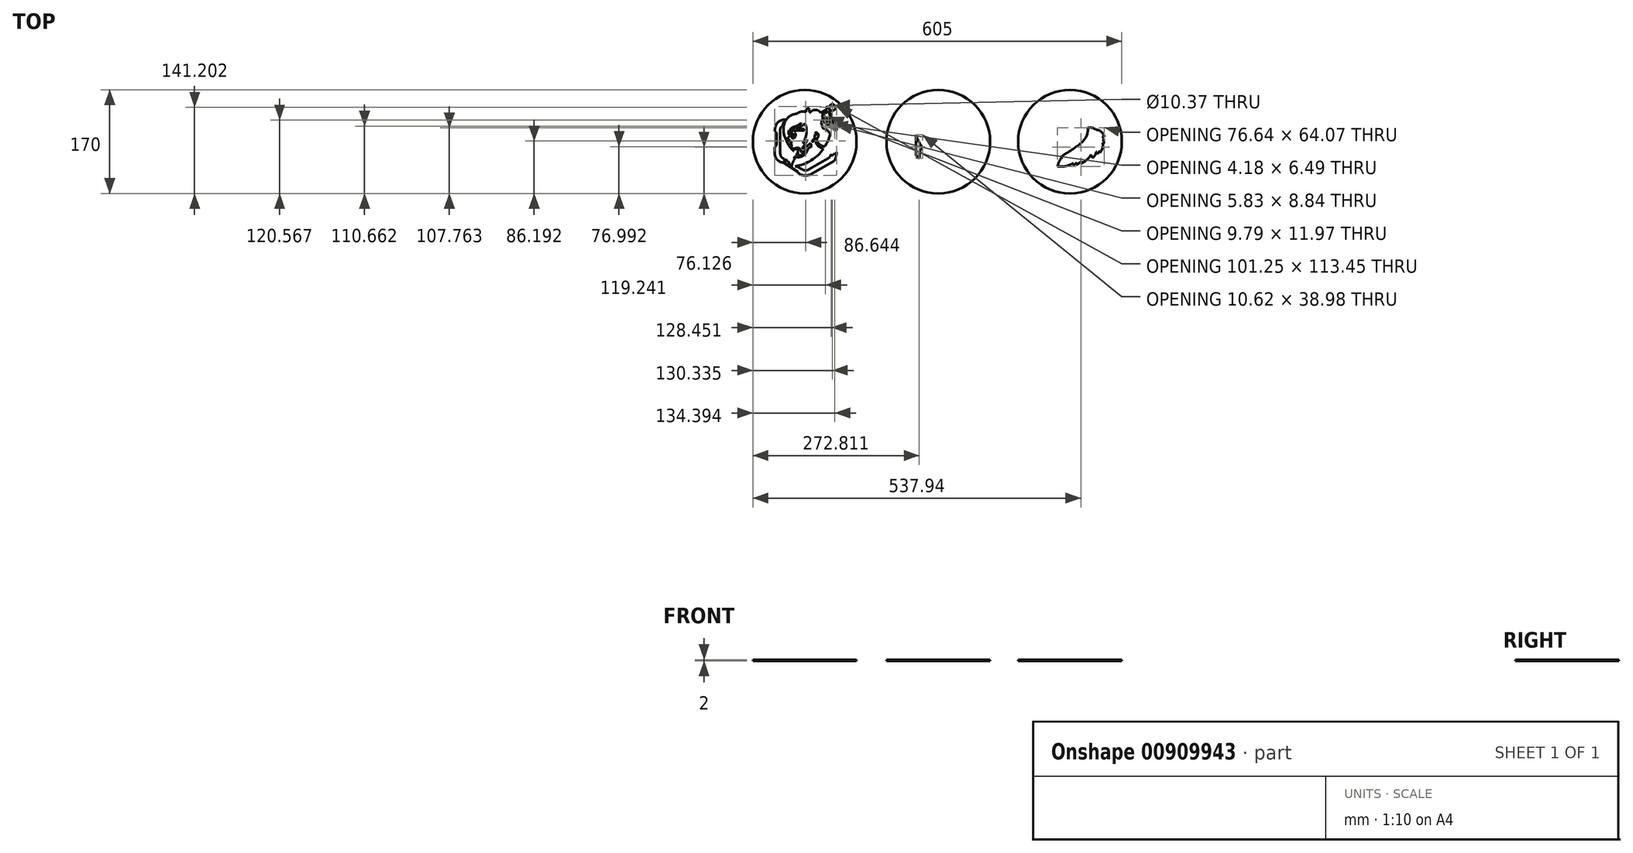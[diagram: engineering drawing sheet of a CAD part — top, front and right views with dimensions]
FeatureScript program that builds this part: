
annotation { "Feature Type Name" : "Feature", "Feature Type Description" : "" }
export const myFeature = defineFeature(function(context is Context, id is Id, definition is map)
    precondition{}
    {
        {
            var Q0;
            Q0=qCreatedBy(makeId("Top.planeOp"),FACE);
            var sketch = newSketch(context, id + "F0", { "sketchPlane" : qUnion([Q0])});
            skArc(sketch, "E0", {"start": v(2.98, 20.38) * mm, "mid": v(2.27, 25.4) * mm, "end": v(0, 29.95) * mm});
            skLineSegment(sketch, "E1", {"start": v(-0.76, 20.69) * mm, "end": v(-13.48, 21.74) * mm});
            skLineSegment(sketch, "E2", {"start": v(-13.48, 21.74) * mm, "end": v(-13.48, 22.74) * mm});
            skLineSegment(sketch, "E3", {"start": v(-13.48, 22.74) * mm, "end": v(-19.26, 22.4) * mm});
            skArc(sketch, "E4", {"start": v(-19.26, 22.4) * mm, "mid": v(-20.2, 21.9) * mm, "end": v(-20.45, 20.84) * mm});
            skArc(sketch, "E5", {"start": v(-20.45, 20.84) * mm, "mid": v(-21.5, 20.38) * mm, "end": v(-22.23, 19.5) * mm});
            skArc(sketch, "E6", {"start": v(-22.91, 18.23) * mm, "mid": v(-22.3, 18.72) * mm, "end": v(-22.23, 19.5) * mm});
            skArc(sketch, "E7", {"start": v(-23.6, 19.5) * mm, "mid": v(-23.46, 18.75) * mm, "end": v(-22.91, 18.23) * mm});
            skArc(sketch, "E8", {"start": v(-24.08, 19.84) * mm, "mid": v(-23.94, 19.54) * mm, "end": v(-23.6, 19.5) * mm});
            skArc(sketch, "E9", {"start": v(-16.32, 24.77) * mm, "mid": v(-20.62, 22.98) * mm, "end": v(-24.08, 19.84) * mm});
            skArc(sketch, "E10", {"start": v(-16.32, 24.77) * mm, "mid": v(-10.63, 27.32) * mm, "end": v(-5.77, 31.23) * mm});
            skArc(sketch, "E11", {"start": v(-12.06, 23.5) * mm, "mid": v(-8.03, 26.64) * mm, "end": v(-5.77, 31.23) * mm});
            skArc(sketch, "E12", {"start": v(-12.06, 23.5) * mm, "mid": v(-5.35, 25.44) * mm, "end": v(0, 29.95) * mm});
            skArc(sketch, "E13", {"start": v(-3.23, -2.27) * mm, "mid": v(1.52, 6.95) * mm, "end": v(3.03, 17.2) * mm});
            skArc(sketch, "E14", {"start": v(-3.23, -2.27) * mm, "mid": v(1.12, -0.57) * mm, "end": v(4.2, 2.96) * mm});
            skArc(sketch, "E15", {"start": v(-4.8, -11.32) * mm, "mid": v(0.43, -4.63) * mm, "end": v(4.2, 2.96) * mm});
            skArc(sketch, "E16", {"start": v(-4.8, -11.32) * mm, "mid": v(3.01, -7.8) * mm, "end": v(9.56, -2.27) * mm});
            skArc(sketch, "E17", {"start": v(9.56, -2.27) * mm, "mid": v(9.67, -2.93) * mm, "end": v(9.82, -3.57) * mm});
            skArc(sketch, "E18", {"start": v(29.41, 22.54) * mm, "mid": v(28.46, 27.03) * mm, "end": v(26.58, 31.23) * mm});
            skArc(sketch, "E19", {"start": v(26.58, 31.23) * mm, "mid": v(29.35, 37.4) * mm, "end": v(28.2, 44.07) * mm});
            skLineSegment(sketch, "E20", {"start": v(28.2, 44.07) * mm, "end": v(38.69, 50.4) * mm});
            skLineSegment(sketch, "E21", {"start": v(38.69, 50.4) * mm, "end": v(40.82, 46.88) * mm});
            skLineSegment(sketch, "E22", {"start": v(40.82, 46.88) * mm, "end": v(42.94, 48.16) * mm});
            skLineSegment(sketch, "E23", {"start": v(42.94, 48.16) * mm, "end": v(38.69, 57.92) * mm});
            skLineSegment(sketch, "E24", {"start": v(38.69, 57.92) * mm, "end": v(35.35, 56.46) * mm});
            skArc(sketch, "E25", {"start": v(35.35, 56.46) * mm, "mid": v(35.57, 55.64) * mm, "end": v(36.4, 55.44) * mm});
            skArc(sketch, "E26", {"start": v(36.4, 53.18) * mm, "mid": v(36.82, 54.31) * mm, "end": v(36.4, 55.44) * mm});
            skLineSegment(sketch, "E27", {"start": v(36.4, 53.18) * mm, "end": v(26.24, 47.39) * mm});
            skArc(sketch, "E28", {"start": v(26.24, 47.39) * mm, "mid": v(17.58, 52.34) * mm, "end": v(8.92, 47.39) * mm});
            skArc(sketch, "E29", {"start": v(7.13, 54.78) * mm, "mid": v(7.26, 50.9) * mm, "end": v(8.92, 47.39) * mm});
            skArc(sketch, "E30", {"start": v(7.13, 54.78) * mm, "mid": v(2.96, 53.06) * mm, "end": v(2.42, 48.6) * mm});
            skArc(sketch, "E31", {"start": v(2.42, 48.6) * mm, "mid": v(-5.84, 49.25) * mm, "end": v(-13.28, 45.63) * mm});
            skArc(sketch, "E32", {"start": v(-13.28, 45.63) * mm, "mid": v(-25.51, 41.11) * mm, "end": v(-33.09, 30.5) * mm});
            skArc(sketch, "E33", {"start": v(-33.09, 30.5) * mm, "mid": v(-34.85, 17.73) * mm, "end": v(-31.54, 5.27) * mm});
            skArc(sketch, "E34", {"start": v(-31.54, 5.27) * mm, "mid": v(-26.16, -5.74) * mm, "end": v(-18.36, -15.2) * mm});
            skArc(sketch, "E35", {"start": v(-18.36, -12.38) * mm, "mid": v(-18.83, -13.79) * mm, "end": v(-18.36, -15.2) * mm});
            skArc(sketch, "E36", {"start": v(-9.8, -12.01) * mm, "mid": v(-14.1, -11.83) * mm, "end": v(-18.36, -12.38) * mm});
            skArc(sketch, "E37", {"start": v(-9.8, -12.01) * mm, "mid": v(-11.09, -16.15) * mm, "end": v(-11.15, -20.49) * mm});
            skArc(sketch, "E38", {"start": v(-12.15, -19.1) * mm, "mid": v(-11.73, -19.85) * mm, "end": v(-11.15, -20.49) * mm});
            skArc(sketch, "E39", {"start": v(-12.15, -19.1) * mm, "mid": v(-12.83, -19.17) * mm, "end": v(-12.84, -19.85) * mm});
            skPoint(sketch, "E39.endSnap0", {"position": v(-11.73, -19.85) * mm});
            skArc(sketch, "E40", {"start": v(-12.45, -21.26) * mm, "mid": v(-12.17, -20.42) * mm, "end": v(-12.84, -19.85) * mm});
            skArc(sketch, "E41", {"start": v(-12.45, -21.26) * mm, "mid": v(-13.16, -21.69) * mm, "end": v(-13.85, -22.17) * mm});
            skLineSegment(sketch, "E42", {"start": v(-17.55, -26.74) * mm, "end": v(-16.32, -26.74) * mm});
            skArc(sketch, "E43", {"start": v(-15.64, -27.26) * mm, "mid": v(-15.9, -26.89) * mm, "end": v(-16.32, -26.74) * mm});
            skArc(sketch, "E44", {"start": v(-15.64, -27.26) * mm, "mid": v(-19.4, -33.43) * mm, "end": v(-21.53, -40.35) * mm});
            skArc(sketch, "E45", {"start": v(-21.53, -40.35) * mm, "mid": v(-22.46, -40.14) * mm, "end": v(-23.4, -40.35) * mm});
            skArc(sketch, "E46", {"start": v(-26.13, -32.33) * mm, "mid": v(-25.18, -36.48) * mm, "end": v(-23.4, -40.35) * mm});
            skArc(sketch, "E47", {"start": v(-15.43, -40.35) * mm, "mid": v(10.63, -30.47) * mm, "end": v(30.92, -11.35) * mm});
            skPoint(sketch, "E47.startSnap0", {"position": v(-15.43, -23.6) * mm});
            skArc(sketch, "E48", {"start": v(41.98, 12.7) * mm, "mid": v(36.6, 18.76) * mm, "end": v(29.41, 22.54) * mm});
            skArc(sketch, "E49", {"start": v(-5.53, -17.95) * mm, "mid": v(-1.98, -15.79) * mm, "end": v(1.56, -13.61) * mm});
            skArc(sketch, "E50", {"start": v(-5.53, -17.95) * mm, "mid": v(-6.68, -13.86) * mm, "end": v(-9.17, -10.41) * mm});
            skArc(sketch, "E51", {"start": v(-9.17, -10.41) * mm, "mid": v(-13.14, -10.14) * mm, "end": v(-16.96, -11.28) * mm});
            skArc(sketch, "E52", {"start": v(-21.82, -7.68) * mm, "mid": v(-20.34, -10.76) * mm, "end": v(-16.96, -11.28) * mm});
            skArc(sketch, "E53", {"start": v(-21.82, -7.68) * mm, "mid": v(-21.6, -5.4) * mm, "end": v(-23.38, -3.97) * mm});
            skArc(sketch, "E54", {"start": v(-20.88, -1.47) * mm, "mid": v(-22.32, -2.53) * mm, "end": v(-23.38, -3.97) * mm});
            skArc(sketch, "E55", {"start": v(-24.72, 0) * mm, "mid": v(-22.93, -1.07) * mm, "end": v(-20.88, -1.47) * mm});
            skArc(sketch, "E56", {"start": v(-24.72, 1.38) * mm, "mid": v(-24.9, 0.69) * mm, "end": v(-24.72, 0) * mm});
            skArc(sketch, "E57", {"start": v(-24.72, 1.38) * mm, "mid": v(-24.75, 2.75) * mm, "end": v(-26, 3.32) * mm});
            skArc(sketch, "E58", {"start": v(-27.8, 5.27) * mm, "mid": v(-27.2, 4.02) * mm, "end": v(-26, 3.32) * mm});
            skArc(sketch, "E59", {"start": v(-27.02, 7) * mm, "mid": v(-27.66, 6.25) * mm, "end": v(-27.8, 5.27) * mm});
            skArc(sketch, "E60", {"start": v(-27.02, 7) * mm, "mid": v(-24.92, 8.65) * mm, "end": v(-23.38, 10.84) * mm});
            skArc(sketch, "E61", {"start": v(-23.38, 10.84) * mm, "mid": v(-23.26, 11.1) * mm, "end": v(-23.16, 11.35) * mm});
            skArc(sketch, "E62", {"start": v(-21.62, 14.34) * mm, "mid": v(-22.16, 14.77) * mm, "end": v(-22.7, 14.34) * mm});
            skArc(sketch, "E63", {"start": v(-20.89, 6.61) * mm, "mid": v(-19.1, 5.43) * mm, "end": v(-17.06, 6.08) * mm});
            skArc(sketch, "E64", {"start": v(-21.62, 14.34) * mm, "mid": v(-21.93, 10.41) * mm, "end": v(-20.89, 6.61) * mm});
            skArc(sketch, "E65", {"start": v(-17.06, 6.08) * mm, "mid": v(-15.29, 9.27) * mm, "end": v(-15.17, 12.93) * mm});
            skArc(sketch, "E66", {"start": v(-14.67, 17.82) * mm, "mid": v(-14.93, 17.28) * mm, "end": v(-15.14, 16.7) * mm});
            skArc(sketch, "E67", {"start": v(-12.8, 18.66) * mm, "mid": v(-13.88, 18.56) * mm, "end": v(-14.67, 17.82) * mm});
            skArc(sketch, "E68", {"start": v(-23.8, 17.14) * mm, "mid": v(-24.94, 18.36) * mm, "end": v(-26.16, 17.22) * mm});
            skArc(sketch, "E69", {"start": v(-26.1, 12.66) * mm, "mid": v(-26.07, 12.44) * mm, "end": v(-26, 12.23) * mm});
            skArc(sketch, "E70", {"start": v(-26.16, 17.22) * mm, "mid": v(-26.23, 14.94) * mm, "end": v(-26.1, 12.66) * mm});
            skArc(sketch, "E71", {"start": v(-26, 12.23) * mm, "mid": v(-25.21, 11.3) * mm, "end": v(-24.08, 11.73) * mm});
            skPoint(sketch, "E72.orphan", {"position": v(-26.1, 12.95) * mm});
            skPoint(sketch, "E73.trimOffspring.end.orphan", {"position": v(-26.16, 16.74) * mm});
            skLineSegment(sketch, "E74", {"start": v(-20.98, 18.42) * mm, "end": v(-17.32, 19.65) * mm});
            skArc(sketch, "E75", {"start": v(-16.9, 9.64) * mm, "mid": v(-16.69, 11.85) * mm, "end": v(-16.64, 14.07) * mm});
            skArc(sketch, "E76", {"start": v(-20.98, 18.42) * mm, "mid": v(-21.19, 16.1) * mm, "end": v(-21.11, 13.77) * mm});
            skArc(sketch, "E77", {"start": v(-20.43, 9.46) * mm, "mid": v(-19.92, 8.27) * mm, "end": v(-19.04, 7.32) * mm});
            skArc(sketch, "E78", {"start": v(-21.11, 13.77) * mm, "mid": v(-20.93, 11.59) * mm, "end": v(-20.43, 9.46) * mm});
            skArc(sketch, "E79.trimOffspring", {"start": v(-19.04, 7.32) * mm, "mid": v(-18.14, 7.44) * mm, "end": v(-17.52, 8.1) * mm});
            skArc(sketch, "E80", {"start": v(-17.52, 8.1) * mm, "mid": v(-17.13, 8.83) * mm, "end": v(-16.9, 9.64) * mm});
            skPoint(sketch, "E81.orphan", {"position": v(-18.02, 7.5) * mm});
            skArc(sketch, "E82", {"start": v(20.04, 10.77) * mm, "mid": v(18.73, 11.71) * mm, "end": v(17.12, 11.89) * mm});
            skArc(sketch, "E83", {"start": v(20.04, 10.77) * mm, "mid": v(19.47, 12.9) * mm, "end": v(17.45, 13.8) * mm});
            skArc(sketch, "E84", {"start": v(14.22, 4.55) * mm, "mid": v(15.76, 4.6) * mm, "end": v(16.7, 5.83) * mm});
            skArc(sketch, "E85", {"start": v(17.15, 4.86) * mm, "mid": v(17.04, 5.4) * mm, "end": v(16.7, 5.83) * mm});
            skArc(sketch, "E86", {"start": v(17.15, 4.86) * mm, "mid": v(17.22, 6.61) * mm, "end": v(15.97, 7.85) * mm});
            skArc(sketch, "E87", {"start": v(15.97, 7.85) * mm, "mid": v(16.75, 9.8) * mm, "end": v(17.12, 11.89) * mm});
            skArc(sketch, "E88", {"start": v(12.05, 0.73) * mm, "mid": v(13.2, 2.6) * mm, "end": v(14.22, 4.55) * mm});
            skArc(sketch, "E89", {"start": v(12.05, 0.73) * mm, "mid": v(12.93, 0.14) * mm, "end": v(13.8, 0.73) * mm});
            skArc(sketch, "E90", {"start": v(13.8, 0.73) * mm, "mid": v(14.42, 0.93) * mm, "end": v(15.02, 1.15) * mm});
            skArc(sketch, "E91", {"start": v(20.83, 5.54) * mm, "mid": v(22.22, 8.7) * mm, "end": v(22.26, 12.17) * mm});
            skArc(sketch, "E92", {"start": v(22.26, 12.17) * mm, "mid": v(20.38, 14.41) * mm, "end": v(17.6, 15.3) * mm});
            skArc(sketch, "E93", {"start": v(17.6, 15.3) * mm, "mid": v(17.4, 14.56) * mm, "end": v(17.45, 13.8) * mm});
            skLineSegment(sketch, "E94", {"start": v(-15.43, -40.35) * mm, "end": v(-11.75, -41.2) * mm});
            skLineSegment(sketch, "E95", {"start": v(-11.75, -41.2) * mm, "end": v(-3.7, -45.74) * mm});
            skLineSegment(sketch, "E96", {"start": v(7.07, -45.34) * mm, "end": v(38.43, -27.31) * mm});
            skArc(sketch, "E97", {"start": v(-3.7, -45.74) * mm, "mid": v(1.74, -47.07) * mm, "end": v(7.07, -45.34) * mm});
            skArc(sketch, "E98", {"start": v(38.43, -27.31) * mm, "mid": v(41.3, -24.72) * mm, "end": v(42.86, -21.17) * mm});
            skArc(sketch, "E99", {"start": v(42.86, -21.17) * mm, "mid": v(44.47, -22.27) * mm, "end": v(46.43, -22.16) * mm});
            skArc(sketch, "E100", {"start": v(48.13, -20) * mm, "mid": v(46.96, -20.83) * mm, "end": v(46.43, -22.16) * mm});
            skArc(sketch, "E101", {"start": v(48.13, -20) * mm, "mid": v(50.42, -20.15) * mm, "end": v(51.7, -18.24) * mm});
            skArc(sketch, "E102", {"start": v(52.27, -17.15) * mm, "mid": v(51.92, -17.66) * mm, "end": v(51.7, -18.24) * mm});
            skArc(sketch, "E103", {"start": v(49.39, -30.3) * mm, "mid": v(51.58, -23.9) * mm, "end": v(52.27, -17.15) * mm});
            skArc(sketch, "E104", {"start": v(47.66, -31.65) * mm, "mid": v(48.54, -31) * mm, "end": v(49.39, -30.3) * mm});
            skLineSegment(sketch, "E105", {"start": v(47.66, -31.65) * mm, "end": v(13.51, -51.26) * mm});
            skLineSegment(sketch, "E106", {"start": v(-10.87, -51.18) * mm, "end": v(-10.87, -49.26) * mm});
            skLineSegment(sketch, "E107", {"start": v(-10.87, -49.26) * mm, "end": v(-34.95, -34.47) * mm});
            skArc(sketch, "E108", {"start": v(-10.87, -51.18) * mm, "mid": v(1.3, -55.53) * mm, "end": v(13.51, -51.26) * mm});
            skArc(sketch, "E109", {"start": v(-28.4, -31.22) * mm, "mid": v(-27.79, -32.85) * mm, "end": v(-26.13, -32.33) * mm});
            skLineSegment(sketch, "E110", {"start": v(-28.4, -31.22) * mm, "end": v(-32.07, -28.94) * mm});
            skArc(sketch, "E111", {"start": v(-32.07, -33.34) * mm, "mid": v(-31.9, -31.14) * mm, "end": v(-32.07, -28.94) * mm});
            skArc(sketch, "E112", {"start": v(-33.86, -32.4) * mm, "mid": v(-33.43, -33.75) * mm, "end": v(-32.07, -33.34) * mm});
            skArc(sketch, "E113", {"start": v(-33.86, -32.4) * mm, "mid": v(-33.53, -30.33) * mm, "end": v(-33.53, -28.24) * mm});
            skArc(sketch, "E114", {"start": v(-40.08, -19.22) * mm, "mid": v(-38.34, -24.84) * mm, "end": v(-33.53, -28.24) * mm});
            skLineSegment(sketch, "E115", {"start": v(-40.08, -19.22) * mm, "end": v(-40.08, 20.21) * mm});
            skArc(sketch, "E116", {"start": v(-35.96, 26.09) * mm, "mid": v(-38.95, 23.8) * mm, "end": v(-40.08, 20.21) * mm});
            skArc(sketch, "E117", {"start": v(-31.67, 36) * mm, "mid": v(-34.72, 31.43) * mm, "end": v(-35.96, 26.09) * mm});
            skArc(sketch, "E118", {"start": v(-31.67, 36) * mm, "mid": v(-42.48, 33.1) * mm, "end": v(-48.25, 23.52) * mm});
            skArc(sketch, "E119", {"start": v(-48.25, 23.52) * mm, "mid": v(-48.78, 21) * mm, "end": v(-48.98, 18.44) * mm});
            skLineSegment(sketch, "E120", {"start": v(-48.98, 18.44) * mm, "end": v(-47.03, 15.8) * mm});
            skLineSegment(sketch, "E121", {"start": v(-46.25, 13.42) * mm, "end": v(-46.25, -4.36) * mm});
            skLineSegment(sketch, "E122", {"start": v(-47.3, -7.06) * mm, "end": v(-48.98, -8.9) * mm});
            skLineSegment(sketch, "E123", {"start": v(-48.98, -8.9) * mm, "end": v(-48.98, -19.22) * mm});
            skArc(sketch, "E124", {"start": v(-48.98, -19.22) * mm, "mid": v(-44.94, -29.58) * mm, "end": v(-34.95, -34.47) * mm});
            skPoint(sketch, "E125.visualSharp", {"position": v(-46.25, -5.91) * mm});
            skArc(sketch, "E125.filletArc", {"start": v(-47.3, -7.06) * mm, "mid": v(-46.52, -5.8) * mm, "end": v(-46.25, -4.36) * mm});
            skPoint(sketch, "E126.visualSharp", {"position": v(-46.25, 14.74) * mm});
            skArc(sketch, "E126.filletArc", {"start": v(-46.25, 13.42) * mm, "mid": v(-46.45, 14.67) * mm, "end": v(-47.03, 15.8) * mm});
            skCircle(sketch, "E127", {"center": v(45.33, 56.2) * mm, "radius": 5.19 * mm});
            skCircle(sketch, "E128", {"center": v(41.71, 45.04) * mm, "radius": 1.43 * mm});
            skCircle(sketch, "E129", {"center": v(42.55, 40.8) * mm, "radius": 1.63 * mm});
            skCircle(sketch, "E130", {"center": v(42.73, 30.59) * mm, "radius": 1.36 * mm});
            skArc(sketch, "E131", {"start": v(39.12, 32.51) * mm, "mid": v(37.28, 30.85) * mm, "end": v(35.75, 28.9) * mm});
            skArc(sketch, "E132", {"start": v(40.66, 31.51) * mm, "mid": v(39.97, 32.14) * mm, "end": v(39.12, 32.51) * mm});
            skArc(sketch, "E133", {"start": v(40.66, 31.51) * mm, "mid": v(40.66, 30.6) * mm, "end": v(41.1, 29.8) * mm});
            skArc(sketch, "E134", {"start": v(41.1, 29.8) * mm, "mid": v(39.97, 28.87) * mm, "end": v(39.12, 27.69) * mm});
            skArc(sketch, "E135", {"start": v(35.75, 28.9) * mm, "mid": v(37.4, 28.17) * mm, "end": v(39.12, 27.69) * mm});
            skArc(sketch, "E136", {"start": v(42.1, 28.17) * mm, "mid": v(41.71, 26.84) * mm, "end": v(41.36, 25.5) * mm});
            skPoint(sketch, "E136.startSnap0", {"position": v(37.4, 28.17) * mm});
            skArc(sketch, "E137", {"start": v(41.36, 25.5) * mm, "mid": v(42.57, 23.76) * mm, "end": v(44.21, 22.42) * mm});
            skArc(sketch, "E138", {"start": v(44.21, 22.42) * mm, "mid": v(45.09, 24.22) * mm, "end": v(45.54, 26.17) * mm});
            skArc(sketch, "E139", {"start": v(44.21, 28.9) * mm, "mid": v(44.77, 27.48) * mm, "end": v(45.54, 26.17) * mm});
            skArc(sketch, "E140", {"start": v(42.1, 28.17) * mm, "mid": v(43.26, 28.25) * mm, "end": v(44.21, 28.9) * mm});
            skArc(sketch, "E141", {"start": v(45.07, 30.19) * mm, "mid": v(46.37, 29.49) * mm, "end": v(47.73, 28.9) * mm});
            skArc(sketch, "E142", {"start": v(47.73, 28.9) * mm, "mid": v(49.73, 30.45) * mm, "end": v(51.2, 32.51) * mm});
            skArc(sketch, "E143", {"start": v(51.2, 32.51) * mm, "mid": v(49.53, 33.36) * mm, "end": v(47.73, 33.85) * mm});
            skArc(sketch, "E144", {"start": v(47.73, 33.85) * mm, "mid": v(46.31, 33.03) * mm, "end": v(45, 32.06) * mm});
            skArc(sketch, "E145", {"start": v(45.07, 30.19) * mm, "mid": v(45.1, 31.12) * mm, "end": v(45, 32.06) * mm});
            skArc(sketch, "E146", {"start": v(43.31, 33.2) * mm, "mid": v(42.7, 33.42) * mm, "end": v(42.1, 33.15) * mm});
            skArc(sketch, "E147", {"start": v(43.31, 33.2) * mm, "mid": v(43.94, 34.66) * mm, "end": v(44.21, 36.23) * mm});
            skArc(sketch, "E148", {"start": v(42.96, 38.5) * mm, "mid": v(43.41, 37.27) * mm, "end": v(44.21, 36.23) * mm});
            skArc(sketch, "E149", {"start": v(42.96, 38.5) * mm, "mid": v(41.83, 37.21) * mm, "end": v(41.36, 35.57) * mm});
            skArc(sketch, "E150", {"start": v(41.36, 35.57) * mm, "mid": v(41.73, 34.36) * mm, "end": v(42.1, 33.15) * mm});
            skLineSegment(sketch, "E151", {"start": v(41.52, 29.05) * mm, "end": v(39.41, 27.26) * mm});
            skLineSegment(sketch, "E152", {"start": v(39.41, 27.26) * mm, "end": v(39.41, 25.7) * mm});
            skLineSegment(sketch, "E153", {"start": v(39.41, 25.7) * mm, "end": v(40.74, 25.7) * mm});
            skArc(sketch, "E154", {"start": v(41.52, 29.05) * mm, "mid": v(41.1, 27.38) * mm, "end": v(40.74, 25.7) * mm});
            skLineSegment(sketch, "E155", {"start": v(38.98, 33.46) * mm, "end": v(41.36, 32.14) * mm});
            skPoint(sketch, "E155.endSnap0", {"position": v(39.97, 32.14) * mm});
            skLineSegment(sketch, "E156", {"start": v(41.36, 32.14) * mm, "end": v(40.66, 35.06) * mm});
            skLineSegment(sketch, "E157", {"start": v(40.66, 35.06) * mm, "end": v(39.1, 35.18) * mm});
            skLineSegment(sketch, "E158", {"start": v(39.1, 35.18) * mm, "end": v(38.98, 33.46) * mm});
            skLineSegment(sketch, "E159", {"start": v(43.94, 32.53) * mm, "end": v(44.64, 36) * mm});
            skLineSegment(sketch, "E160", {"start": v(44.64, 36) * mm, "end": v(47.12, 37.22) * mm});
            skLineSegment(sketch, "E161", {"start": v(47.12, 37.22) * mm, "end": v(47.06, 34.87) * mm});
            skLineSegment(sketch, "E162", {"start": v(47.06, 34.87) * mm, "end": v(43.94, 32.53) * mm});
            skLineSegment(sketch, "E163", {"start": v(44.71, 29.28) * mm, "end": v(47.75, 28.1) * mm});
            skLineSegment(sketch, "E164", {"start": v(47.75, 28.1) * mm, "end": v(48.1, 26.46) * mm});
            skLineSegment(sketch, "E165", {"start": v(48.1, 26.46) * mm, "end": v(46.18, 26.41) * mm});
            skLineSegment(sketch, "E166", {"start": v(46.18, 26.41) * mm, "end": v(44.71, 29.28) * mm});
            skArc(sketch, "E167", {"start": v(52.1, 19.14) * mm, "mid": v(52.07, 23.35) * mm, "end": v(50.32, 27.19) * mm});
            skArc(sketch, "E168", {"start": v(48.02, 24.8) * mm, "mid": v(49.82, 25.37) * mm, "end": v(50.32, 27.19) * mm});
            skArc(sketch, "E169", {"start": v(48.02, 24.8) * mm, "mid": v(46.7, 23.05) * mm, "end": v(46.57, 20.87) * mm});
            skArc(sketch, "E170", {"start": v(51.44, 18.34) * mm, "mid": v(49.12, 19.83) * mm, "end": v(46.57, 20.87) * mm});
            skArc(sketch, "E171", {"start": v(51.44, 18.34) * mm, "mid": v(51.85, 18.67) * mm, "end": v(52.1, 19.14) * mm});
            skArc(sketch, "E172", {"start": v(33.69, 29.58) * mm, "mid": v(35.54, 31.33) * mm, "end": v(37.04, 33.4) * mm});
            skArc(sketch, "E173", {"start": v(39.14, 36.78) * mm, "mid": v(37.07, 35.72) * mm, "end": v(37.04, 33.4) * mm});
            skArc(sketch, "E174", {"start": v(29.34, 31.9) * mm, "mid": v(30.9, 36.6) * mm, "end": v(30.73, 41.55) * mm});
            skLineSegment(sketch, "E175", {"start": v(29.34, 31.9) * mm, "end": v(33.69, 29.58) * mm});
            skLineSegment(sketch, "E176", {"start": v(39.14, 36.78) * mm, "end": v(30.73, 41.55) * mm});
            skCircle(sketch, "E177", {"center": v(0, 0) * mm, "radius": 85 * mm});
            skArc(sketch, "E178", {"start": v(-13.85, -22.17) * mm, "mid": v(-4.3, -21.21) * mm, "end": v(1.56, -13.61) * mm});
            skArc(sketch, "E179", {"start": v(-16.37, -24.74) * mm, "mid": v(-2.5, -22.97) * mm, "end": v(5.23, -11.33) * mm});
            skArc(sketch, "E180.trimOffspring", {"start": v(5.23, -11.33) * mm, "mid": v(8.49, -9.28) * mm, "end": v(11.74, -7.22) * mm});
            skArc(sketch, "E181.trimOffspring", {"start": v(-16.37, -24.74) * mm, "mid": v(-17.01, -25.71) * mm, "end": v(-17.55, -26.74) * mm});
            skPoint(sketch, "E182.endSnap0", {"position": v(10.92, -3.1) * mm});
            skArc(sketch, "E183.trimOffspring", {"start": v(15.86, 1.53) * mm, "mid": v(16.84, 2.05) * mm, "end": v(17.77, 2.64) * mm});
            skArc(sketch, "E184.trimOffspring", {"start": v(9.95, -4.03) * mm, "mid": v(10.69, -5.71) * mm, "end": v(11.74, -7.22) * mm});
            skLineSegment(sketch, "E185", {"start": v(-16.77, 16.23) * mm, "end": v(-15.14, 16.7) * mm});
            skArc(sketch, "E186.trimOffspring", {"start": v(-16.77, 16.23) * mm, "mid": v(-17, 17.94) * mm, "end": v(-17.32, 19.65) * mm});
            skLineSegment(sketch, "E187", {"start": v(-23.83, 13.2) * mm, "end": v(-22.72, 13.2) * mm});
            skArc(sketch, "E188.trimOffspring", {"start": v(-22.72, 13.2) * mm, "mid": v(-22.68, 13.77) * mm, "end": v(-22.7, 14.34) * mm});
            skArc(sketch, "E189.trimOffspring", {"start": v(-23.83, 13.2) * mm, "mid": v(-23.75, 15.17) * mm, "end": v(-23.8, 17.14) * mm});
            skArc(sketch, "E190", {"start": v(3.03, 17.2) * mm, "mid": v(3.07, 18.8) * mm, "end": v(2.98, 20.38) * mm});
            skLineSegment(sketch, "E191", {"start": v(15.02, 1.15) * mm, "end": v(15.86, 1.53) * mm});
            skLineSegment(sketch, "E192", {"start": v(9.82, -3.57) * mm, "end": v(9.95, -4.03) * mm});
            skLineSegment(sketch, "E193", {"start": v(-16.64, 14.07) * mm, "end": v(-15.4, 14.07) * mm});
            skLineSegment(sketch, "E194", {"start": v(-0.76, 20.69) * mm, "end": v(-0.76, 17.55) * mm});
            skLineSegment(sketch, "E195", {"start": v(-12.8, 18.66) * mm, "end": v(-0.76, 17.55) * mm});
            skLineSegment(sketch, "E196", {"start": v(-24.08, 11.73) * mm, "end": v(-23.16, 11.35) * mm});
            skPoint(sketch, "E182.end.orphan", {"position": v(12.16, -3.1) * mm});
            skPoint(sketch, "E197.orphan", {"position": v(12.03, -2.64) * mm});
            skArc(sketch, "E198", {"start": v(17.77, 2.64) * mm, "mid": v(21.83, -6.71) * mm, "end": v(30.92, -11.35) * mm});
            skArc(sketch, "E199", {"start": v(19.8, 4.36) * mm, "mid": v(24.21, -4.32) * mm, "end": v(33.35, -7.7) * mm});
            skArc(sketch, "E200.trimOffspring", {"start": v(33.35, -7.7) * mm, "mid": v(38.46, 2.16) * mm, "end": v(41.98, 12.7) * mm});
            skArc(sketch, "E201.trimOffspring", {"start": v(19.8, 4.36) * mm, "mid": v(20.33, 4.94) * mm, "end": v(20.83, 5.54) * mm});
            skLineSegment(sketch, "E202", {"start": v(-15.4, 14.07) * mm, "end": v(-15.17, 12.93) * mm});
            skSolve(sketch);
        }
        {
            var Q0;
            Q0=makeQuery(id+"F0.imprint","IMPRINT",FACE,{"disambiguationData":[TD([[makeQuery(id+"F0.imprint","IMPRINT",EDGE,{"derivedFrom":sQuery(id+"F0.wireOp",EDGE,"E13")}),1.0]])]});
            var Q1;
            Q1=makeQuery(id+"F0.imprint","IMPRINT",FACE,{"disambiguationData":[TD([[makeQuery(id+"F0.imprint","IMPRINT",EDGE,{"derivedFrom":sQuery(id+"F0.wireOp",EDGE,"E0")}),1.0]])]});
            var Q2;
            Q2=makeQuery(id+"F0.imprint","IMPRINT",FACE,{"disambiguationData":[TD([[makeQuery(id+"F0.imprint","IMPRINT",EDGE,{"derivedFrom":sQuery(id+"F0.wireOp",EDGE,"E18")}),-1.0]])]});
            var Q3;
            Q3=makeQuery(id+"F0.imprint","IMPRINT",FACE,{"disambiguationData":[TD([[makeQuery(id+"F0.imprint","IMPRINT",EDGE,{"derivedFrom":sQuery(id+"F0.wireOp",EDGE,"E74")}),-1.0]])]});
            var Q4;
            {var subQ4=sQuery(id+"F0.wireOp",EDGE,"E68");Q4=makeQuery(id+"F0.imprint","IMPRINT",FACE,{"disambiguationData":[TD([[makeQuery(id+"F0.imprint","IMPRINT",EDGE,{"derivedFrom":subQ4}),1.0]])]});}
            var Q5;
            Q5=makeQuery(id+"F0.imprint","IMPRINT",FACE,{"disambiguationData":[TD([[makeQuery(id+"F0.imprint","IMPRINT",EDGE,{"derivedFrom":sQuery(id+"F0.wireOp",EDGE,"E82")}),1.0]])]});
            extrude(context, id + "F1", {"entities" : qUnion([Q0, Q1, Q2, Q3, Q4, Q5]), "depth" : 2 * mm, "offsetDistance" : 25 * mm});
        }
        {
            var Q0;
            Q0=makeQuery(id+"F1.opExtrude","SWEPT_BODY",BODY,{"disambiguationData":[OSD([sQuery(id+"F0.wireOp",EDGE,"E0"),sQuery(id+"F0.wireOp",EDGE,"E1"),sQuery(id+"F0.wireOp",EDGE,"E2"),sQuery(id+"F0.wireOp",EDGE,"E3"),sQuery(id+"F0.wireOp",EDGE,"E4"),sQuery(id+"F0.wireOp",EDGE,"E5"),sQuery(id+"F0.wireOp",EDGE,"E6"),sQuery(id+"F0.wireOp",EDGE,"E7"),sQuery(id+"F0.wireOp",EDGE,"E8"),sQuery(id+"F0.wireOp",EDGE,"E9"),sQuery(id+"F0.wireOp",EDGE,"E10"),sQuery(id+"F0.wireOp",EDGE,"E11"),sQuery(id+"F0.wireOp",EDGE,"E12"),sQuery(id+"F0.wireOp",EDGE,"E13"),sQuery(id+"F0.wireOp",EDGE,"E14"),sQuery(id+"F0.wireOp",EDGE,"E15"),sQuery(id+"F0.wireOp",EDGE,"E16"),sQuery(id+"F0.wireOp",EDGE,"E17"),sQuery(id+"F0.wireOp",EDGE,"E18"),sQuery(id+"F0.wireOp",EDGE,"E19"),sQuery(id+"F0.wireOp",EDGE,"E20"),sQuery(id+"F0.wireOp",EDGE,"E21"),sQuery(id+"F0.wireOp",EDGE,"E22"),sQuery(id+"F0.wireOp",EDGE,"E23"),sQuery(id+"F0.wireOp",EDGE,"E24"),sQuery(id+"F0.wireOp",EDGE,"E25"),sQuery(id+"F0.wireOp",EDGE,"E26"),sQuery(id+"F0.wireOp",EDGE,"E27"),sQuery(id+"F0.wireOp",EDGE,"E28"),sQuery(id+"F0.wireOp",EDGE,"E29"),sQuery(id+"F0.wireOp",EDGE,"E30"),sQuery(id+"F0.wireOp",EDGE,"E31"),sQuery(id+"F0.wireOp",EDGE,"E32"),sQuery(id+"F0.wireOp",EDGE,"E33"),sQuery(id+"F0.wireOp",EDGE,"E34"),sQuery(id+"F0.wireOp",EDGE,"E35"),sQuery(id+"F0.wireOp",EDGE,"E36"),sQuery(id+"F0.wireOp",EDGE,"E37"),sQuery(id+"F0.wireOp",EDGE,"E38"),sQuery(id+"F0.wireOp",EDGE,"E39"),sQuery(id+"F0.wireOp",EDGE,"E40"),sQuery(id+"F0.wireOp",EDGE,"E41"),sQuery(id+"F0.wireOp",EDGE,"E42"),sQuery(id+"F0.wireOp",EDGE,"E43"),sQuery(id+"F0.wireOp",EDGE,"E44"),sQuery(id+"F0.wireOp",EDGE,"E45"),sQuery(id+"F0.wireOp",EDGE,"E46"),sQuery(id+"F0.wireOp",EDGE,"E47"),sQuery(id+"F0.wireOp",EDGE,"E48"),sQuery(id+"F0.wireOp",EDGE,"E49"),sQuery(id+"F0.wireOp",EDGE,"E50"),sQuery(id+"F0.wireOp",EDGE,"E51"),sQuery(id+"F0.wireOp",EDGE,"E52"),sQuery(id+"F0.wireOp",EDGE,"E53"),sQuery(id+"F0.wireOp",EDGE,"E54"),sQuery(id+"F0.wireOp",EDGE,"E55"),sQuery(id+"F0.wireOp",EDGE,"E56"),sQuery(id+"F0.wireOp",EDGE,"E57"),sQuery(id+"F0.wireOp",EDGE,"E58"),sQuery(id+"F0.wireOp",EDGE,"E59"),sQuery(id+"F0.wireOp",EDGE,"E60"),sQuery(id+"F0.wireOp",EDGE,"E61"),sQuery(id+"F0.wireOp",EDGE,"E62"),sQuery(id+"F0.wireOp",EDGE,"E63"),sQuery(id+"F0.wireOp",EDGE,"E64"),sQuery(id+"F0.wireOp",EDGE,"E65"),sQuery(id+"F0.wireOp",EDGE,"E66"),sQuery(id+"F0.wireOp",EDGE,"E67"),sQuery(id+"F0.wireOp",EDGE,"jZ2bbEK5-KPZT-Isj0-lUX8-zPC80vGDEggy"),sQuery(id+"F0.wireOp",EDGE,"E68"),sQuery(id+"F0.wireOp",EDGE,"E69"),sQuery(id+"F0.wireOp",EDGE,"E70"),sQuery(id+"F0.wireOp",EDGE,"cz1Zz00t-M5O7-Bdo5-LgHU-c5VUJpIl8gsS"),sQuery(id+"F0.wireOp",EDGE,"E71"),sQuery(id+"F0.wireOp",EDGE,"E74"),sQuery(id+"F0.wireOp",EDGE,"E75"),sQuery(id+"F0.wireOp",EDGE,"E76"),sQuery(id+"F0.wireOp",EDGE,"E77"),sQuery(id+"F0.wireOp",EDGE,"E78"),sQuery(id+"F0.wireOp",EDGE,"E79.trimOffspring"),sQuery(id+"F0.wireOp",EDGE,"E80"),sQuery(id+"F0.wireOp",EDGE,"E82"),sQuery(id+"F0.wireOp",EDGE,"E83"),sQuery(id+"F0.wireOp",EDGE,"E84"),sQuery(id+"F0.wireOp",EDGE,"E85"),sQuery(id+"F0.wireOp",EDGE,"E86"),sQuery(id+"F0.wireOp",EDGE,"E87"),sQuery(id+"F0.wireOp",EDGE,"E88"),sQuery(id+"F0.wireOp",EDGE,"E89"),sQuery(id+"F0.wireOp",EDGE,"E90"),sQuery(id+"F0.wireOp",EDGE,"E91"),sQuery(id+"F0.wireOp",EDGE,"E92"),sQuery(id+"F0.wireOp",EDGE,"E93"),sQuery(id+"F0.wireOp",EDGE,"E94"),sQuery(id+"F0.wireOp",EDGE,"E95"),sQuery(id+"F0.wireOp",EDGE,"E96"),sQuery(id+"F0.wireOp",EDGE,"E97"),sQuery(id+"F0.wireOp",EDGE,"E98"),sQuery(id+"F0.wireOp",EDGE,"E99"),sQuery(id+"F0.wireOp",EDGE,"E100"),sQuery(id+"F0.wireOp",EDGE,"E101"),sQuery(id+"F0.wireOp",EDGE,"E102"),sQuery(id+"F0.wireOp",EDGE,"E103"),sQuery(id+"F0.wireOp",EDGE,"E104"),sQuery(id+"F0.wireOp",EDGE,"E105"),sQuery(id+"F0.wireOp",EDGE,"E106"),sQuery(id+"F0.wireOp",EDGE,"E107"),sQuery(id+"F0.wireOp",EDGE,"E108"),sQuery(id+"F0.wireOp",EDGE,"E109"),sQuery(id+"F0.wireOp",EDGE,"E110"),sQuery(id+"F0.wireOp",EDGE,"E111"),sQuery(id+"F0.wireOp",EDGE,"E112"),sQuery(id+"F0.wireOp",EDGE,"E113"),sQuery(id+"F0.wireOp",EDGE,"E114"),sQuery(id+"F0.wireOp",EDGE,"E115"),sQuery(id+"F0.wireOp",EDGE,"E116"),sQuery(id+"F0.wireOp",EDGE,"E117"),sQuery(id+"F0.wireOp",EDGE,"E118"),sQuery(id+"F0.wireOp",EDGE,"E119"),sQuery(id+"F0.wireOp",EDGE,"E120"),sQuery(id+"F0.wireOp",EDGE,"E121"),sQuery(id+"F0.wireOp",EDGE,"E122"),sQuery(id+"F0.wireOp",EDGE,"E123"),sQuery(id+"F0.wireOp",EDGE,"E124"),sQuery(id+"F0.wireOp",EDGE,"E125.filletArc"),sQuery(id+"F0.wireOp",EDGE,"E126.filletArc"),sQuery(id+"F0.wireOp",EDGE,"E127"),sQuery(id+"F0.wireOp",EDGE,"E128"),sQuery(id+"F0.wireOp",EDGE,"E129"),sQuery(id+"F0.wireOp",EDGE,"E130"),sQuery(id+"F0.wireOp",EDGE,"E131"),sQuery(id+"F0.wireOp",EDGE,"E132"),sQuery(id+"F0.wireOp",EDGE,"E133"),sQuery(id+"F0.wireOp",EDGE,"E134"),sQuery(id+"F0.wireOp",EDGE,"E135"),sQuery(id+"F0.wireOp",EDGE,"E136"),sQuery(id+"F0.wireOp",EDGE,"E137"),sQuery(id+"F0.wireOp",EDGE,"E138"),sQuery(id+"F0.wireOp",EDGE,"E139"),sQuery(id+"F0.wireOp",EDGE,"E140"),sQuery(id+"F0.wireOp",EDGE,"E141"),sQuery(id+"F0.wireOp",EDGE,"E142"),sQuery(id+"F0.wireOp",EDGE,"E143"),sQuery(id+"F0.wireOp",EDGE,"E144"),sQuery(id+"F0.wireOp",EDGE,"E145"),sQuery(id+"F0.wireOp",EDGE,"E146"),sQuery(id+"F0.wireOp",EDGE,"E147"),sQuery(id+"F0.wireOp",EDGE,"E148"),sQuery(id+"F0.wireOp",EDGE,"E149"),sQuery(id+"F0.wireOp",EDGE,"E150"),sQuery(id+"F0.wireOp",EDGE,"E151"),sQuery(id+"F0.wireOp",EDGE,"E152"),sQuery(id+"F0.wireOp",EDGE,"E153"),sQuery(id+"F0.wireOp",EDGE,"E154"),sQuery(id+"F0.wireOp",EDGE,"E155"),sQuery(id+"F0.wireOp",EDGE,"E156"),sQuery(id+"F0.wireOp",EDGE,"E157"),sQuery(id+"F0.wireOp",EDGE,"E158"),sQuery(id+"F0.wireOp",EDGE,"E159"),sQuery(id+"F0.wireOp",EDGE,"E160"),sQuery(id+"F0.wireOp",EDGE,"E161"),sQuery(id+"F0.wireOp",EDGE,"E162"),sQuery(id+"F0.wireOp",EDGE,"E163"),sQuery(id+"F0.wireOp",EDGE,"E164"),sQuery(id+"F0.wireOp",EDGE,"E165"),sQuery(id+"F0.wireOp",EDGE,"E166"),sQuery(id+"F0.wireOp",EDGE,"E167"),sQuery(id+"F0.wireOp",EDGE,"E168"),sQuery(id+"F0.wireOp",EDGE,"E169"),sQuery(id+"F0.wireOp",EDGE,"E170"),sQuery(id+"F0.wireOp",EDGE,"E171"),sQuery(id+"F0.wireOp",EDGE,"E172"),sQuery(id+"F0.wireOp",EDGE,"E173"),sQuery(id+"F0.wireOp",EDGE,"E174"),sQuery(id+"F0.wireOp",EDGE,"E175"),sQuery(id+"F0.wireOp",EDGE,"E176"),sQuery(id+"F0.wireOp",EDGE,"E177"),sQuery(id+"F0.wireOp",EDGE,"E178"),sQuery(id+"F0.wireOp",EDGE,"E179"),sQuery(id+"F0.wireOp",EDGE,"E180.trimOffspring"),sQuery(id+"F0.wireOp",EDGE,"E181.trimOffspring"),sQuery(id+"F0.wireOp",EDGE,"FUzCqxml-6W96-zn6E-ScAs-83uhb5cPZFK3"),sQuery(id+"F0.wireOp",EDGE,"XJEICPlt-zT1N-TdBw-dwfY-jE3PMoaDvZ3y"),sQuery(id+"F0.wireOp",EDGE,"9jTBkBlY-NBeK-ubw1-dJXg-93La8SPVcOSY"),sQuery(id+"F0.wireOp",EDGE,"E182"),sQuery(id+"F0.wireOp",EDGE,"6RP5Ezp9-CUN0-bkEc-lEvw-ABqGMNCKC1e7"),sQuery(id+"F0.wireOp",EDGE,"ARTNzvJs-8JWv-oLHC-LCMA-xynzKxNTvyzi"),sQuery(id+"F0.wireOp",EDGE,"E183.trimOffspring"),sQuery(id+"F0.wireOp",EDGE,"E184.trimOffspring"),sQuery(id+"F0.wireOp",EDGE,"E185"),sQuery(id+"F0.wireOp",EDGE,"tx7fKw2V-FISJ-uTbj-nAwP-W8jFjnU1NCah"),sQuery(id+"F0.wireOp",EDGE,"b42e9a1e-e5a2-47ae-9383-d2bdd0e25a15.trimOffspring"),sQuery(id+"F0.wireOp",EDGE,"E186.trimOffspring"),sQuery(id+"F0.wireOp",EDGE,"E187"),sQuery(id+"F0.wireOp",EDGE,"M9iZa7HA-BBmy-c3fK-SHbj-Swwr29vpJuGP"),sQuery(id+"F0.wireOp",EDGE,"E188.trimOffspring"),sQuery(id+"F0.wireOp",EDGE,"E189.trimOffspring"),sQuery(id+"F0.wireOp",EDGE,"E190"),sQuery(id+"F0.wireOp",EDGE,"ibqOQRtN-hj0t-ImVl-QG18-0fNQxN3BfLQS")])]});
            transform(context, id + "F2", {"entities" : qUnion([Q0]), "transformType" : TransformType.TRANSLATION_3D, "dx" : -219 * mm, "dy" : 0 * mm, "dz" : 0 * mm, "makeCopy" : false});
        }
        {
            var Q0;
            Q0=qCreatedBy(makeId("Top.planeOp"),FACE);
            var sketch = newSketch(context, id + "F3", { "sketchPlane" : qUnion([Q0])});
            skArc(sketch, "E203", {"start": v(-12.32, -25.23) * mm, "mid": v(-17.64, -32.3) * mm, "end": v(-20.38, -40.7) * mm});
            skArc(sketch, "E204", {"start": v(-20.38, -40.7) * mm, "mid": v(-13.81, -40.87) * mm, "end": v(-7.27, -40.17) * mm});
            skArc(sketch, "E205", {"start": v(-7.27, -40.17) * mm, "mid": v(-0.87, -38.15) * mm, "end": v(5.24, -35.34) * mm});
            skArc(sketch, "E206", {"start": v(5.24, -38.71) * mm, "mid": v(5.5, -37.03) * mm, "end": v(5.24, -35.34) * mm});
            skArc(sketch, "E207", {"start": v(5.24, -38.71) * mm, "mid": v(8.1, -36.94) * mm, "end": v(10.4, -34.48) * mm});
            skArc(sketch, "E208", {"start": v(10.4, -34.48) * mm, "mid": v(10.37, -36.22) * mm, "end": v(11, -37.85) * mm});
            skArc(sketch, "E209", {"start": v(11, -37.85) * mm, "mid": v(15, -35.2) * mm, "end": v(18.48, -31.9) * mm});
            skArc(sketch, "E210", {"start": v(18.48, -31.9) * mm, "mid": v(18.3, -33.77) * mm, "end": v(18.48, -35.64) * mm});
            skArc(sketch, "E211", {"start": v(18.48, -35.64) * mm, "mid": v(27.63, -29.82) * mm, "end": v(34.42, -21.37) * mm});
            skArc(sketch, "E212", {"start": v(36.64, -26.8) * mm, "mid": v(35.74, -24) * mm, "end": v(34.42, -21.37) * mm});
            skArc(sketch, "E213", {"start": v(36.64, -26.8) * mm, "mid": v(40.92, -22.24) * mm, "end": v(43, -16.35) * mm});
            skArc(sketch, "E214", {"start": v(45.07, -20.16) * mm, "mid": v(44.28, -18.12) * mm, "end": v(43, -16.35) * mm});
            skArc(sketch, "E215", {"start": v(45.07, -20.16) * mm, "mid": v(47.12, -17.9) * mm, "end": v(48.35, -15.13) * mm});
            skArc(sketch, "E216", {"start": v(49.3, -18.19) * mm, "mid": v(49.23, -16.53) * mm, "end": v(48.35, -15.13) * mm});
            skArc(sketch, "E217", {"start": v(49.3, -18.19) * mm, "mid": v(53.3, -10.52) * mm, "end": v(53.67, -1.89) * mm});
            skArc(sketch, "E218", {"start": v(55.2, -3.42) * mm, "mid": v(54.64, -2.46) * mm, "end": v(53.67, -1.89) * mm});
            skArc(sketch, "E219", {"start": v(55.2, -3.42) * mm, "mid": v(55.37, -0.08) * mm, "end": v(54.35, 3.1) * mm});
            skArc(sketch, "E220", {"start": v(55.46, 2.31) * mm, "mid": v(55.04, 2.9) * mm, "end": v(54.35, 3.1) * mm});
            skArc(sketch, "E221", {"start": v(55.46, 2.31) * mm, "mid": v(54.78, 5.95) * mm, "end": v(52.93, 9.15) * mm});
            skArc(sketch, "E222", {"start": v(56.26, 8.15) * mm, "mid": v(54.63, 8.76) * mm, "end": v(52.93, 9.15) * mm});
            skArc(sketch, "E223", {"start": v(56.26, 8.15) * mm, "mid": v(51.57, 16.1) * mm, "end": v(43, 19.58) * mm});
            skArc(sketch, "E224", {"start": v(43, 19.58) * mm, "mid": v(36.41, 22.81) * mm, "end": v(29.07, 22.63) * mm});
            skArc(sketch, "E225", {"start": v(20.55, 0) * mm, "mid": v(27.54, 10.29) * mm, "end": v(29.07, 22.63) * mm});
            skArc(sketch, "E226", {"start": v(-4.41, -18.19) * mm, "mid": v(8.47, -9.65) * mm, "end": v(20.55, 0) * mm});
            skArc(sketch, "E227", {"start": v(-4.41, -18.19) * mm, "mid": v(-10.02, -21.45) * mm, "end": v(-15.2, -25.36) * mm});
            skArc(sketch, "E228", {"start": v(-12.32, -25.23) * mm, "mid": v(-13.78, -25.03) * mm, "end": v(-15.2, -25.36) * mm});
            skCircle(sketch, "E229", {"center": v(0, 0) * mm, "radius": 85 * mm});
            skSolve(sketch);
        }
        {
            var Q0;
            Q0=makeQuery(id+"F3.imprint","IMPRINT",FACE,{"disambiguationData":[TD([[makeQuery(id+"F3.imprint","IMPRINT",EDGE,{"derivedFrom":sQuery(id+"F3.wireOp",EDGE,"E203")}),-1.0]])]});
            extrude(context, id + "F4", {"entities" : qUnion([Q0]), "depth" : 2 * mm, "offsetDistance" : 25 * mm});
        }
        {
            var Q0;
            Q0=makeQuery(id+"F4.opExtrude","SWEPT_BODY",BODY,{"disambiguationData":[OSD([sQuery(id+"F3.wireOp",EDGE,"E203"),sQuery(id+"F3.wireOp",EDGE,"E204"),sQuery(id+"F3.wireOp",EDGE,"E205"),sQuery(id+"F3.wireOp",EDGE,"E206"),sQuery(id+"F3.wireOp",EDGE,"E207"),sQuery(id+"F3.wireOp",EDGE,"E208"),sQuery(id+"F3.wireOp",EDGE,"E209"),sQuery(id+"F3.wireOp",EDGE,"E210"),sQuery(id+"F3.wireOp",EDGE,"E211"),sQuery(id+"F3.wireOp",EDGE,"E212"),sQuery(id+"F3.wireOp",EDGE,"E213"),sQuery(id+"F3.wireOp",EDGE,"E214"),sQuery(id+"F3.wireOp",EDGE,"E215"),sQuery(id+"F3.wireOp",EDGE,"E216"),sQuery(id+"F3.wireOp",EDGE,"E217"),sQuery(id+"F3.wireOp",EDGE,"E218"),sQuery(id+"F3.wireOp",EDGE,"E219"),sQuery(id+"F3.wireOp",EDGE,"E220"),sQuery(id+"F3.wireOp",EDGE,"E221"),sQuery(id+"F3.wireOp",EDGE,"E222"),sQuery(id+"F3.wireOp",EDGE,"E223"),sQuery(id+"F3.wireOp",EDGE,"E224"),sQuery(id+"F3.wireOp",EDGE,"E225"),sQuery(id+"F3.wireOp",EDGE,"E226"),sQuery(id+"F3.wireOp",EDGE,"E227"),sQuery(id+"F3.wireOp",EDGE,"E228"),sQuery(id+"F3.wireOp",EDGE,"E229")])]});
            transform(context, id + "F5", {"entities" : qUnion([Q0]), "transformType" : TransformType.TRANSLATION_3D, "dx" : 216 * mm, "dy" : 0 * mm, "dz" : 0 * mm, "makeCopy" : false});
        }
        {
            var Q0;
            Q0=qCreatedBy(makeId("Top.planeOp"),FACE);
            var sketch = newSketch(context, id + "F6", { "sketchPlane" : qUnion([Q0])});
            skArc(sketch, "E230", {"start": v(-36.5, 11.48) * mm, "mid": v(-32.16, 0.48) * mm, "end": v(-25.88, -9.54) * mm});
            skArc(sketch, "E231", {"start": v(-25.88, -9.54) * mm, "mid": v(-30.26, -16.76) * mm, "end": v(-30.46, -25.2) * mm});
            skArc(sketch, "E232", {"start": v(-30.46, -25.2) * mm, "mid": v(-31.97, -26.07) * mm, "end": v(-32.96, -27.5) * mm});
            skArc(sketch, "E233", {"start": v(-32.96, -27.5) * mm, "mid": v(-33.81, -24.62) * mm, "end": v(-36.34, -23.01) * mm});
            skLineSegment(sketch, "E234", {"start": v(-36.34, -23.01) * mm, "end": v(-36.5, 11.48) * mm});
            skCircle(sketch, "E235", {"center": v(0, 0) * mm, "radius": 85 * mm});
            skSolve(sketch);
        }
        {
            var Q0;
            Q0=makeQuery(id+"F6.imprint","IMPRINT",FACE,{"disambiguationData":[TD([[makeQuery(id+"F6.imprint","IMPRINT",EDGE,{"derivedFrom":sQuery(id+"F6.wireOp",EDGE,"E230")}),1.0]])]});
            extrude(context, id + "F7", {"entities" : qUnion([Q0]), "depth" : 2 * mm, "offsetDistance" : 25 * mm});
        }
    });
